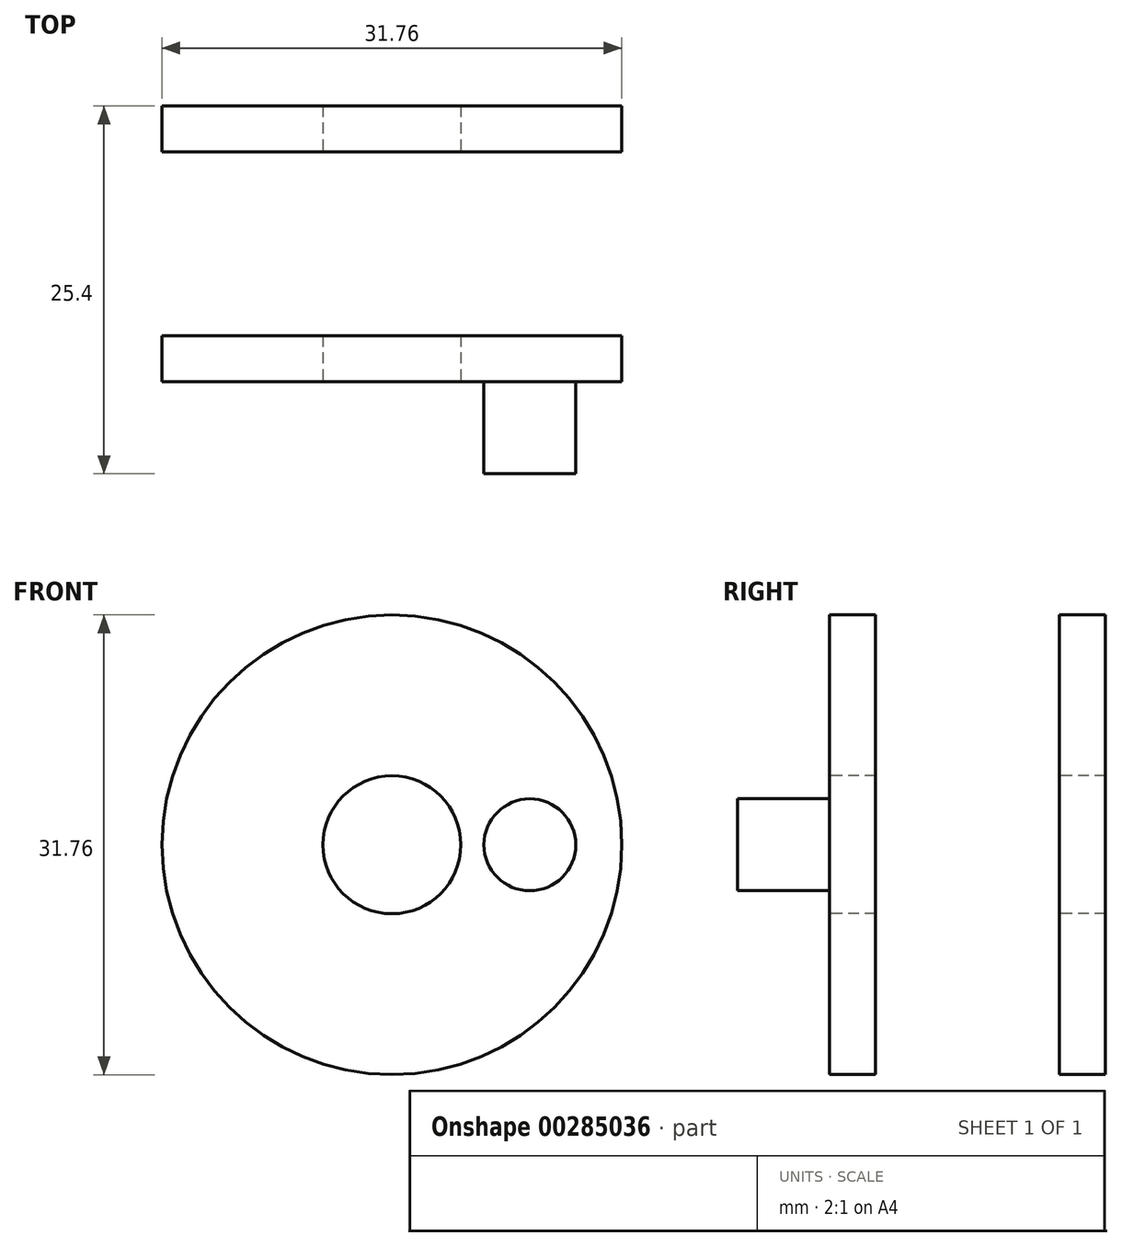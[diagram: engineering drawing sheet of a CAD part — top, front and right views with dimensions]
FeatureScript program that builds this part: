
annotation { "Feature Type Name" : "Feature", "Feature Type Description" : "" }
export const myFeature = defineFeature(function(context is Context, id is Id, definition is map)
    precondition{}
    {
        {
            var Q0;
            Q0=qCreatedBy(makeId("Right.planeOp"),FACE);
            var sketch = newSketch(context, id + "F0", { "sketchPlane" : qUnion([Q0])});
            skLineSegment(sketch, "E0", {"start": v(0, 0) * mm, "end": v(19.05, 0) * mm});
            skLineSegment(sketch, "E1", {"start": v(0, 4.76) * mm, "end": v(19.05, 4.76) * mm});
            skLineSegment(sketch, "E2", {"start": v(0, 4.76) * mm, "end": v(0, 15.88) * mm});
            skLineSegment(sketch, "E3", {"start": v(0, 15.88) * mm, "end": v(3.18, 15.88) * mm});
            skLineSegment(sketch, "E4", {"start": v(3.18, 15.88) * mm, "end": v(3.18, 4.76) * mm});
            skLineSegment(sketch, "E5", {"start": v(19.05, 4.76) * mm, "end": v(19.05, 15.88) * mm});
            skLineSegment(sketch, "E6", {"start": v(19.05, 15.88) * mm, "end": v(15.88, 15.88) * mm});
            skLineSegment(sketch, "E7", {"start": v(15.88, 15.88) * mm, "end": v(15.88, 4.76) * mm});
            skLineSegment(sketch, "E8", {"start": v(3.18, 4.76) * mm, "end": v(3.18, 12.7) * mm});
            skLineSegment(sketch, "E9", {"start": v(3.18, 12.7) * mm, "end": v(15.88, 12.7) * mm});
            skSolve(sketch);
        }
        {
            var Q0;
            {var subQ3=sQuery(id+"F0.wireOp",EDGE,"E5");Q0=makeQuery(id+"F0.imprint","IMPRINT",FACE,{"disambiguationData":[TD([[makeQuery(id+"F0.imprint","IMPRINT",EDGE,{"derivedFrom":subQ3}),1.0]])]});}
            var Q1;
            {var subQ3=sQuery(id+"F0.wireOp",EDGE,"E8");Q1=makeQuery(id+"F0.imprint","IMPRINT",FACE,{"disambiguationData":[TD([[makeQuery(id+"F0.imprint","IMPRINT",EDGE,{"derivedFrom":subQ3}),-1.0]])]});}
            var Q2;
            {var subQ0=sQuery(id+"F0.wireOp",EDGE,"E2");Q2=makeQuery(id+"F0.imprint","IMPRINT",FACE,{"disambiguationData":[TD([[makeQuery(id+"F0.imprint","IMPRINT",EDGE,{"derivedFrom":subQ0}),-1.0]])]});}
            var Q3;
            Q3=sQuery(id+"F0.wireOp",EDGE,"E0");
            revolve(context, id + "F1", {"entities" : qUnion([Q0, Q1, Q2]), "axis" : qUnion([Q3]), "revolveType" : RevolveType.FULL});
        }
        {
            var Q0;
            Q0=qCreatedBy(makeId("Front.planeOp"),FACE);
            var sketch = newSketch(context, id + "F2", { "sketchPlane" : qUnion([Q0])});
            skCircle(sketch, "E10", {"center": v(9.53, 0) * mm, "radius": 3.18 * mm});
            skSolve(sketch);
        }
        {
            var Q0;
            Q0 = qSketchRegion(id + "F2", true);
            extrude(context, id + "F3", {"entities" : qUnion([Q0]), "operationType" : NewBodyOperationType.ADD, "depth" : 6.35 * mm});
        }
    });
